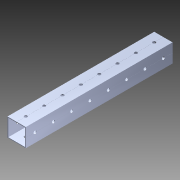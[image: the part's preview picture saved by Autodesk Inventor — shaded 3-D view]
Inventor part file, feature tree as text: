
AUTODESK INVENTOR PART (.ipt)
format: ipt  version: 2014 (Build 180170000, 170)  size: 1,221,632 bytes
history: native  units: in
note: dims shown in document units (in); Inventor stores cm internally (conversion verified against a paired STEP export)
features: extrude x2, sketch x2, pattern_circular x1, other x1, imported_body x1
ambient origin geometry x8: Origin, YZ Plane, XZ Plane, XY Plane, X Axis, Y Axis, Z Axis, Center Point
bodies: Body1 (feature_tree)
feature tree (7):
  pattern_circular  "CirPattern2"
  other  "1x1 tube1"
  extrude  "Extrusion1"  Depth=1.0in TaperAngle=0.0deg
  extrude  "Extrusion2"  [1 undecoded]
  imported_body  "Base1"
  sketch  "Sketch1"  dims[d0=50.0in d1=0.0in d2=1.0in d3=0.0in]
  sketch  "Sketch3"
note: 1 required parameter value undecoded (feature->parameter linkage not recoverable at this tier; creation-order binding heuristic only, values carry confidence <= 0.55)
